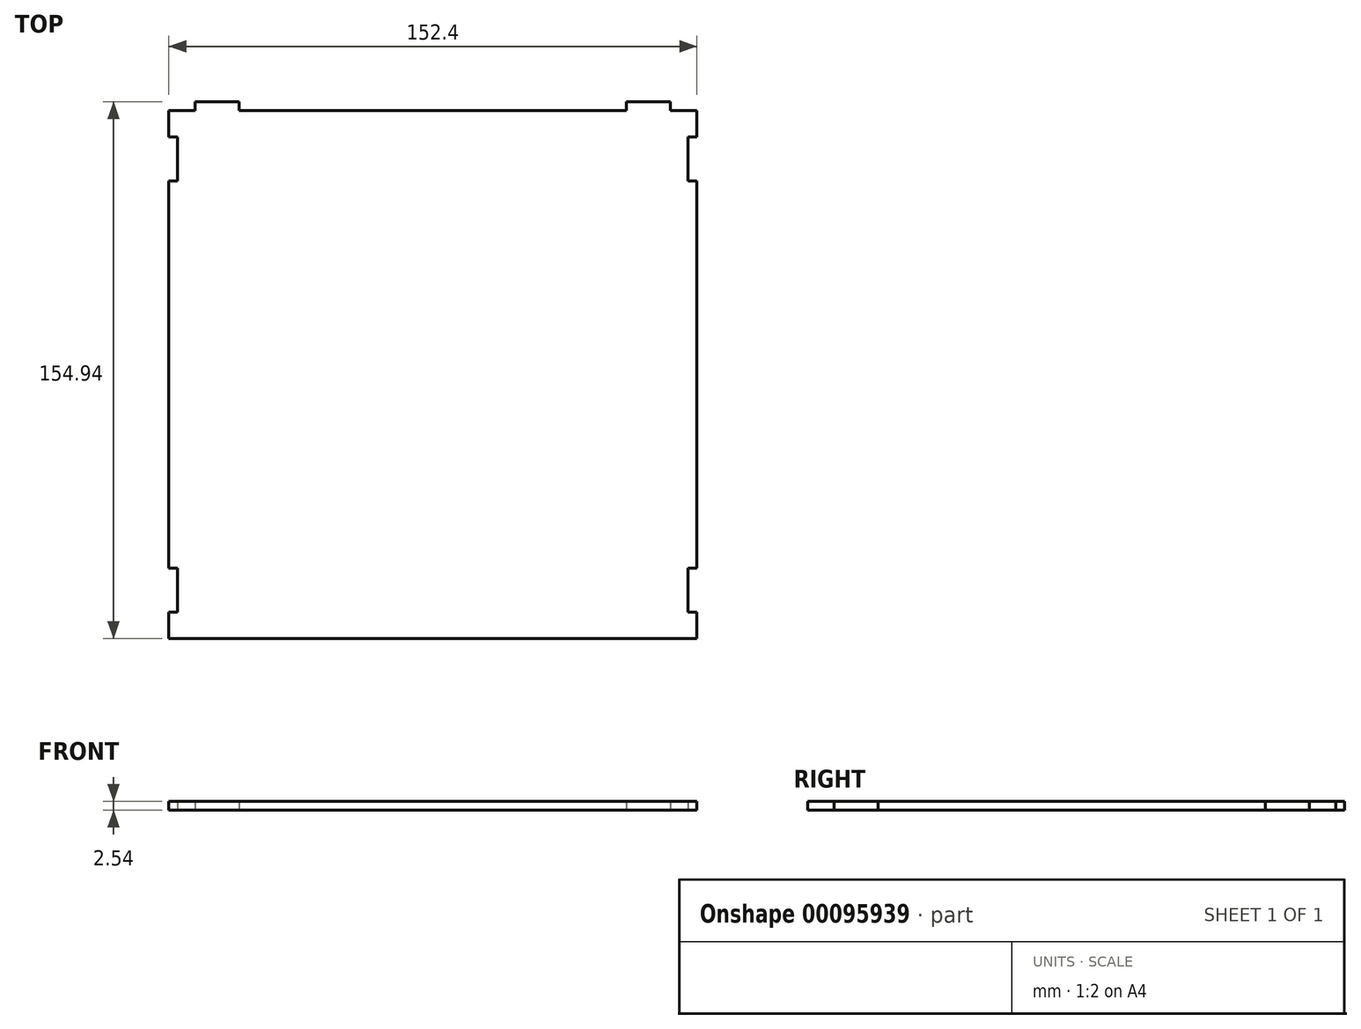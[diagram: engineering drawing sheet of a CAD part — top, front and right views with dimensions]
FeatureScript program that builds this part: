
annotation { "Feature Type Name" : "Feature", "Feature Type Description" : "" }
export const myFeature = defineFeature(function(context is Context, id is Id, definition is map)
    precondition{}
    {
        {
            var Q0;
            Q0=qCreatedBy(makeId("Top.planeOp"),FACE);
            var sketch = newSketch(context, id + "F0", { "sketchPlane" : qUnion([Q0])});
            skLineSegment(sketch, "E0.top", {"start": v(76.2, -76.2) * mm, "end": v(-76.2, -76.2) * mm});
            skLineSegment(sketch, "E0.left", {"start": v(76.2, 76.2) * mm, "end": v(76.2, -76.2) * mm});
            skLineSegment(sketch, "E0.right", {"start": v(-76.2, 76.2) * mm, "end": v(-76.2, -76.2) * mm});
            skPoint(sketch, "E0.middle", {"position": v(0, 0) * mm});
            skLineSegment(sketch, "E1.top", {"start": v(-68.58, 78.74) * mm, "end": v(-55.88, 78.74) * mm});
            skLineSegment(sketch, "E1.left", {"start": v(-68.58, 76.2) * mm, "end": v(-68.58, 78.74) * mm});
            skLineSegment(sketch, "E1.right", {"start": v(-55.88, 76.2) * mm, "end": v(-55.88, 78.74) * mm});
            skLineSegment(sketch, "E2.MirrorCS", {"start": v(55.88, 76.2) * mm, "end": v(55.88, 78.74) * mm});
            skLineSegment(sketch, "E3.MirrorCS", {"start": v(68.58, 78.74) * mm, "end": v(55.88, 78.74) * mm});
            skLineSegment(sketch, "E4.MirrorCS", {"start": v(68.58, 76.2) * mm, "end": v(68.58, 78.74) * mm});
            skLineSegment(sketch, "E5.bottom", {"start": v(-76.2, 68.58) * mm, "end": v(-73.66, 68.58) * mm});
            skLineSegment(sketch, "E5.top", {"start": v(-76.2, 55.88) * mm, "end": v(-73.66, 55.88) * mm});
            skLineSegment(sketch, "E5.left", {"start": v(-76.2, 68.58) * mm, "end": v(-76.2, 55.88) * mm});
            skLineSegment(sketch, "E5.right", {"start": v(-73.66, 68.58) * mm, "end": v(-73.66, 55.88) * mm});
            skLineSegment(sketch, "E6.MirrorCS", {"start": v(76.2, 55.88) * mm, "end": v(73.66, 55.88) * mm});
            skLineSegment(sketch, "E7.MirrorCS", {"start": v(73.66, 68.58) * mm, "end": v(73.66, 55.88) * mm});
            skLineSegment(sketch, "E8.MirrorCS", {"start": v(76.2, 68.58) * mm, "end": v(73.66, 68.58) * mm});
            skLineSegment(sketch, "E9.MirrorCS", {"start": v(76.2, -55.88) * mm, "end": v(73.66, -55.88) * mm});
            skLineSegment(sketch, "E10.MirrorCS", {"start": v(73.66, -68.58) * mm, "end": v(73.66, -55.88) * mm});
            skLineSegment(sketch, "E11.MirrorCS", {"start": v(76.2, -68.58) * mm, "end": v(73.66, -68.58) * mm});
            skLineSegment(sketch, "E12.MirrorCS", {"start": v(-76.2, -55.88) * mm, "end": v(-73.66, -55.88) * mm});
            skLineSegment(sketch, "E13.MirrorCS", {"start": v(-73.66, -68.58) * mm, "end": v(-73.66, -55.88) * mm});
            skLineSegment(sketch, "E14.MirrorCS", {"start": v(-76.2, -68.58) * mm, "end": v(-73.66, -68.58) * mm});
            skLineSegment(sketch, "E15", {"start": v(-76.2, 76.2) * mm, "end": v(-68.58, 76.2) * mm});
            skLineSegment(sketch, "E16", {"start": v(-55.88, 76.2) * mm, "end": v(55.88, 76.2) * mm});
            skLineSegment(sketch, "E17", {"start": v(68.58, 76.2) * mm, "end": v(76.2, 76.2) * mm});
            skSolve(sketch);
        }
        {
            var Q0;
            {var subQ6=sQuery(id+"F0.wireOp",EDGE,"E0.top");Q0=makeQuery(id+"F0.imprint","IMPRINT",FACE,{"disambiguationData":[TD([[makeQuery(id+"F0.imprint","IMPRINT",EDGE,{"derivedFrom":subQ6}),-1.0]])]});}
            extrude(context, id + "F1", {"entities" : qUnion([Q0]), "depth" : 2.54 * mm});
        }
    });
